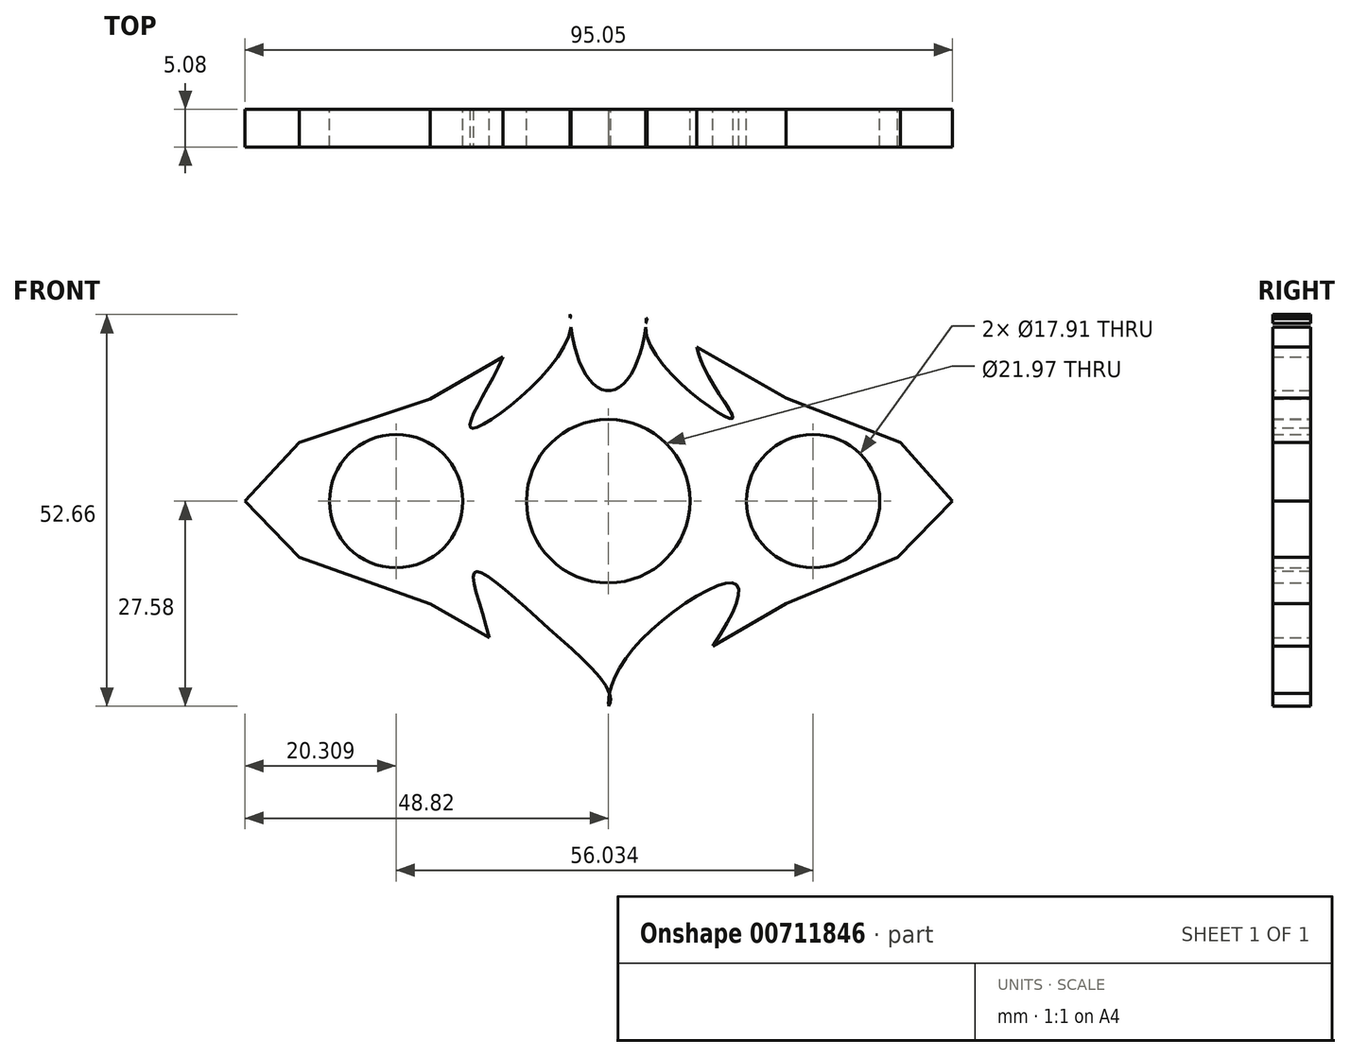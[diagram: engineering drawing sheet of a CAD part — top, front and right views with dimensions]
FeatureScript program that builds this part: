
annotation { "Feature Type Name" : "Feature", "Feature Type Description" : "" }
export const myFeature = defineFeature(function(context is Context, id is Id, definition is map)
    precondition{}
    {
        {
            var Q0;
            Q0=qCreatedBy(makeId("Front.planeOp"),FACE);
            var sketch = newSketch(context, id + "F0", { "sketchPlane" : qUnion([Q0])});
            skCircle(sketch, "E0.cCircle", {"center": v(0, 0) * mm, "radius": 23.88 * mm, "construction": true});
            skLineSegment(sketch, "E0.0", {"start": v(-0.06, 27.58) * mm, "end": v(23.85, 13.84) * mm});
            skLineSegment(sketch, "E0.1", {"start": v(23.85, 13.84) * mm, "end": v(23.9, -13.74) * mm});
            skLineSegment(sketch, "E0.2", {"start": v(23.9, -13.74) * mm, "end": v(0.06, -27.58) * mm});
            skLineSegment(sketch, "E0.3", {"start": v(0.06, -27.58) * mm, "end": v(-23.85, -13.84) * mm});
            skLineSegment(sketch, "E0.4", {"start": v(-23.85, -13.84) * mm, "end": v(-23.9, 13.74) * mm});
            skLineSegment(sketch, "E0.5", {"start": v(-23.9, 13.74) * mm, "end": v(-0.06, 27.58) * mm});
            skPoint(sketch, "E0.0.midPoint", {"position": v(11.9, 20.7) * mm});
            skCircle(sketch, "E1", {"center": v(0, 0) * mm, "radius": 10.99 * mm});
            skEllipse(sketch, "E2", {"center": v(0, 26.15) * mm, "majorRadius": 11.31 * mm, "minorRadius": 5.16 * mm, "majorAxis": v(0, 1)});
            skFitSpline(sketch, "E3", {"points": [v(0.06, -27.58) * mm, v(4.84, -18.23) * mm, v(17.03, -11.06) * mm, v(14.22, -19.19) * mm, v(2.07, -30.04) * mm, v(0.06, -27.58) * mm]});
            skFitSpline(sketch, "E4", {"points": [v(0.06, -27.58) * mm, v(-7.86, -17.22) * mm, v(-17.91, -9.55) * mm, v(-15.98, -18.36) * mm, v(-11.12, -28.91) * mm, v(0.06, -27.58) * mm]});
            skFitSpline(sketch, "E5", {"points": [v(-14.18, 19.38) * mm, v(-18.33, 9.79) * mm, v(-5, 23.35) * mm, v(-9.7, 28.3) * mm, v(-14.18, 19.38) * mm]});
            skFitSpline(sketch, "E6", {"points": [v(11.9, 20.7) * mm, v(16.61, 11.09) * mm, v(5, 23.35) * mm, v(11.9, 28.24) * mm, v(11.9, 20.7) * mm]});
            skLineSegment(sketch, "E7", {"start": v(-44.6, 4.68) * mm, "end": v(-44.6, -2.39) * mm});
            skLineSegment(sketch, "E8", {"start": v(41.56, 4.68) * mm, "end": v(41.57, 0) * mm});
            skCircle(sketch, "E9", {"center": v(27.52, 0) * mm, "radius": 8.95 * mm});
            skCircle(sketch, "E10", {"center": v(-28.51, 0) * mm, "radius": 8.95 * mm});
            skLineSegment(sketch, "E11", {"start": v(-44.6, 0) * mm, "end": v(41.57, 0.17) * mm});
            skLineSegment(sketch, "E12", {"start": v(-23.9, 13.74) * mm, "end": v(-41.54, 7.87) * mm});
            skLineSegment(sketch, "E13", {"start": v(-41.54, 7.87) * mm, "end": v(-44.6, 4.68) * mm});
            skLineSegment(sketch, "E14", {"start": v(-44.6, -2.39) * mm, "end": v(-41.54, -7.57) * mm});
            skLineSegment(sketch, "E15", {"start": v(-41.54, -7.57) * mm, "end": v(-23.85, -13.84) * mm});
            skLineSegment(sketch, "E16", {"start": v(41.57, 0) * mm, "end": v(38.89, -7.57) * mm});
            skLineSegment(sketch, "E17", {"start": v(38.89, -7.57) * mm, "end": v(23.9, -13.74) * mm});
            skLineSegment(sketch, "E18", {"start": v(41.56, 4.68) * mm, "end": v(39.26, 7.87) * mm});
            skLineSegment(sketch, "E19", {"start": v(39.26, 7.87) * mm, "end": v(23.85, 13.84) * mm});
            skLineSegment(sketch, "E20", {"start": v(-41.54, 7.87) * mm, "end": v(-48.82, 0) * mm});
            skLineSegment(sketch, "E21", {"start": v(-48.82, 0) * mm, "end": v(-41.54, -7.57) * mm});
            skLineSegment(sketch, "E22", {"start": v(39.26, 7.87) * mm, "end": v(46.23, 0) * mm});
            skLineSegment(sketch, "E23", {"start": v(46.23, 0) * mm, "end": v(38.89, -7.57) * mm});
            skSolve(sketch);
        }
        {
            var Q0;
            {var subQ0=sQuery(id+"F0.wireOp",EDGE,"E2");var subQ1=sQuery(id+"F0.wireOp",EDGE,"E0.0");var subQ2=makeQuery(id+"F0.imprint","INTERSECT",VERTEX,{"derivedFrom":[subQ1,subQ0]});Q0=makeQuery(id+"F0.imprint","IMPRINT",FACE,{"disambiguationData":[TD([[makeQuery(id+"F0.imprint","IMPRINT",EDGE,{"disambiguationData":[TD([[subQ2,-1.0]])],"derivedFrom":subQ1}),-1.0]])]});}
            var Q1;
            {var subQ0=sQuery(id+"F0.wireOp",EDGE,"E4");var subQ1=sQuery(id+"F0.wireOp",EDGE,"E3");var subQ3=makeQuery(id+"F0.imprint","INTERSECT",VERTEX,{"derivedFrom":[subQ1,subQ0]});Q1=makeQuery(id+"F0.imprint","IMPRINT",FACE,{"disambiguationData":[TD([[makeQuery(id+"F0.imprint","IMPRINT",EDGE,{"disambiguationData":[TD([[subQ3,1.0]])],"derivedFrom":subQ1}),-1.0]])]});}
            var Q2;
            {var subQ5=sQuery(id+"F0.wireOp",EDGE,"E18");Q2=makeQuery(id+"F0.imprint","IMPRINT",FACE,{"disambiguationData":[TD([[makeQuery(id+"F0.imprint","IMPRINT",EDGE,{"derivedFrom":subQ5}),1.0]])]});}
            var Q3;
            {var subQ7=sQuery(id+"F0.wireOp",EDGE,"E16");Q3=makeQuery(id+"F0.imprint","IMPRINT",FACE,{"disambiguationData":[TD([[makeQuery(id+"F0.imprint","IMPRINT",EDGE,{"derivedFrom":subQ7}),-1.0]])]});}
            var Q4;
            {var subQ5=sQuery(id+"F0.wireOp",EDGE,"E14");Q4=makeQuery(id+"F0.imprint","IMPRINT",FACE,{"disambiguationData":[TD([[makeQuery(id+"F0.imprint","IMPRINT",EDGE,{"derivedFrom":subQ5}),1.0]])]});}
            var Q5;
            {var subQ7=sQuery(id+"F0.wireOp",EDGE,"E12");Q5=makeQuery(id+"F0.imprint","IMPRINT",FACE,{"disambiguationData":[TD([[makeQuery(id+"F0.imprint","IMPRINT",EDGE,{"derivedFrom":subQ7}),1.0]])]});}
            var Q6;
            {var subQ0=sQuery(id+"F0.wireOp",EDGE,"E2");var subQ1=sQuery(id+"F0.wireOp",EDGE,"E0.5");var subQ2=makeQuery(id+"F0.imprint","INTERSECT",VERTEX,{"derivedFrom":[subQ1,subQ0]});Q6=makeQuery(id+"F0.imprint","IMPRINT",FACE,{"disambiguationData":[TD([[makeQuery(id+"F0.imprint","IMPRINT",EDGE,{"disambiguationData":[TD([[subQ2,-1.0]])],"derivedFrom":subQ1}),1.0]])]});}
            var Q7;
            {var subQ5=sQuery(id+"F0.wireOp",EDGE,"E11");var subQ6=sQuery(id+"F0.wireOp",EDGE,"E1");var subQ15=makeQuery(id+"F0.imprint","INTERSECT",VERTEX,{"disambiguationData":[OD(0.0)],"derivedFrom":[subQ6,subQ5]});Q7=makeQuery(id+"F0.imprint","IMPRINT",FACE,{"disambiguationData":[TD([[makeQuery(id+"F0.imprint","IMPRINT",EDGE,{"disambiguationData":[TD([[subQ15,-1.0]])],"derivedFrom":subQ6}),-1.0]])]});}
            var Q8;
            {var subQ0=sQuery(id+"F0.wireOp",EDGE,"E11");var subQ3=sQuery(id+"F0.wireOp",EDGE,"E1");var subQ4=makeQuery(id+"F0.imprint","INTERSECT",VERTEX,{"disambiguationData":[OD(0.0)],"derivedFrom":[subQ3,subQ0]});Q8=makeQuery(id+"F0.imprint","IMPRINT",FACE,{"disambiguationData":[TD([[makeQuery(id+"F0.imprint","IMPRINT",EDGE,{"disambiguationData":[TD([[subQ4,1.0]])],"derivedFrom":subQ3}),-1.0]])]});}
            var Q9;
            {var subQ1=sQuery(id+"F0.wireOp",EDGE,"E16");Q9=makeQuery(id+"F0.imprint","IMPRINT",FACE,{"disambiguationData":[TD([[makeQuery(id+"F0.imprint","IMPRINT",EDGE,{"derivedFrom":subQ1}),1.0]])]});}
            var Q10;
            {var subQ3=sQuery(id+"F0.wireOp",EDGE,"E13");Q10=makeQuery(id+"F0.imprint","IMPRINT",FACE,{"disambiguationData":[TD([[makeQuery(id+"F0.imprint","IMPRINT",EDGE,{"derivedFrom":subQ3}),-1.0]])]});}
            var Q11;
            {var subQ0=sQuery(id+"F0.wireOp",EDGE,"E14");Q11=makeQuery(id+"F0.imprint","IMPRINT",FACE,{"disambiguationData":[TD([[makeQuery(id+"F0.imprint","IMPRINT",EDGE,{"derivedFrom":subQ0}),-1.0]])]});}
            extrude(context, id + "F1", {"entities" : qUnion([Q0, Q1, Q2, Q3, Q4, Q5, Q6, Q7, Q8, Q9, Q10, Q11]), "depth" : 5.08 * mm, "offsetDistance" : 25.4 * mm});
        }
    });
